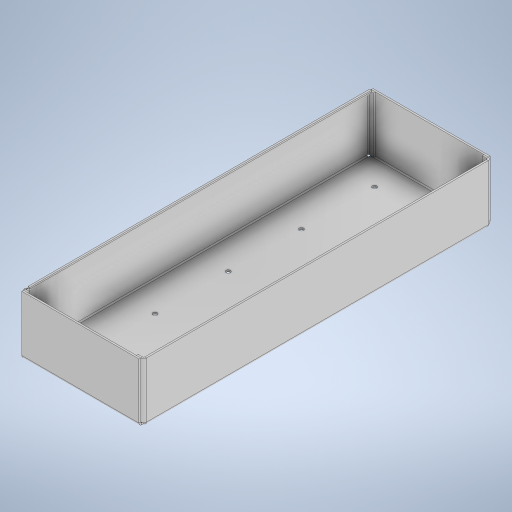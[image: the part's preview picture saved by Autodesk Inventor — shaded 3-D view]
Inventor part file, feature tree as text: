
AUTODESK INVENTOR PART (.ipt)
format: ipt  version: 2023 (Build 270158000, 158)  size: 450,560 bytes
history: native  units: in
note: dims shown in document units (in); Inventor stores cm internally (conversion verified against a paired STEP export)
features: sheet_metal_op x16, sketch x11, other x8, hole x1, pattern_linear x1
ambient origin geometry x8: Origin, YZ Plane, XZ Plane, XY Plane, X Axis, Y Axis, Z Axis, Center Point
bodies: Solid1 (feature_tree)
feature tree (37):
  sheet_metal_op  "Face1"
  hole  "Hole1"  [1 undecoded]
  pattern_linear  "Rectangular Pattern1"  Count1=30  [1 undecoded]
  sheet_metal_op  "Flange4"
  sheet_metal_op  "Flange5"
  sheet_metal_op  "Flange6"
  sketch  "Sketch13"  dims[d14=0.7874in d16=3.937in]
  sketch  "Sketch14"  dims[d17=1.9685in d19=4.9213in]
  sheet_metal_op  "Flange9"
  sheet_metal_op  "Flange10"
  sketch  "Sketch1"  dims[d0=23.622in d1=7.874in d2=11.811in]
  other  "Plate1"
  sketch  "Sketch2"  dims[d3=3.937in]
  sketch  "Sketch6"  dims[d4=0.12in]
  other  "Plate5"
  sheet_metal_op  "Bend4"
  sheet_metal_op  "Corner4"
  sketch  "Sketch7"  dims[d5=0.2969in d6=0.2953in d7=0.1476in d8=0.0984in d9=90.0deg d10=0.12in]
  other  "Plate6"
  sheet_metal_op  "Bend5"
  sheet_metal_op  "Corner5"
  sketch  "Sketch8"  dims[d11=0.0in]
  sketch  "Sketch9"  dims[d12=1.9685in]
  sketch  "Sketch10"  dims[d13=2.0669in]
  other  "Plate7"
  sheet_metal_op  "Bend6"
  sheet_metal_op  "Corner6"
  sketch  "Sketch15"  dims[d50=0.12in]
  other  "Plate10"
  sheet_metal_op  "Bend9"
  sheet_metal_op  "Corner9"
  sketch  "Sketch16"  dims[d51=0.06in d52=0.24in d53=0.12in d54=3.937in d55=90.0deg d56=0.0787in d57=0.48in d58=0.12in d59=0.12in d60=0.12in d61=0.06in d62=0.24in d63=0.12in d64=3.937in d65=90.0deg d66=0.0787in d67=0.48in d68=0.12in d69=0.12in d70=0.0433in d71=0.0787in d72=0.0433in d73=0.0787in d76=0.1987in d77=0.1987in d78=0.12in d79=0.0in d80=0.12in d81=0.0in d82=0.12in d83=0.06in d84=0.24in d85=0.12in d86=0.4921in d87=90.0deg d88=0.0787in d89=0.48in d90=0.12in d91=0.12in d116=0.1575in d117=0.12in d118=0.1575in d119=0.12in d120=0.1376in d121=0.0787in d122=0.1757in d123=0.12in d124=0.06in d125=0.06in d126=0.06in d127=0.12in d128=0.06in d129=0.24in d130=0.12in d131=0.2953in d132=90.0deg d133=0.0787in d134=0.48in d135=0.12in d136=0.12in d137=0.12in d138=0.06in d139=0.24in d140=0.12in d141=0.2953in d142=90.0deg d143=0.0787in d144=0.48in d145=0.12in d146=0.12in]
  other  "Plate11"
  sheet_metal_op  "Bend10"
  sheet_metal_op  "Corner10"
  other  "Cut2"
  other  "Cut3"
note: 2 required parameter values undecoded (feature->parameter linkage not recoverable at this tier; creation-order binding heuristic only, values carry confidence <= 0.55)
